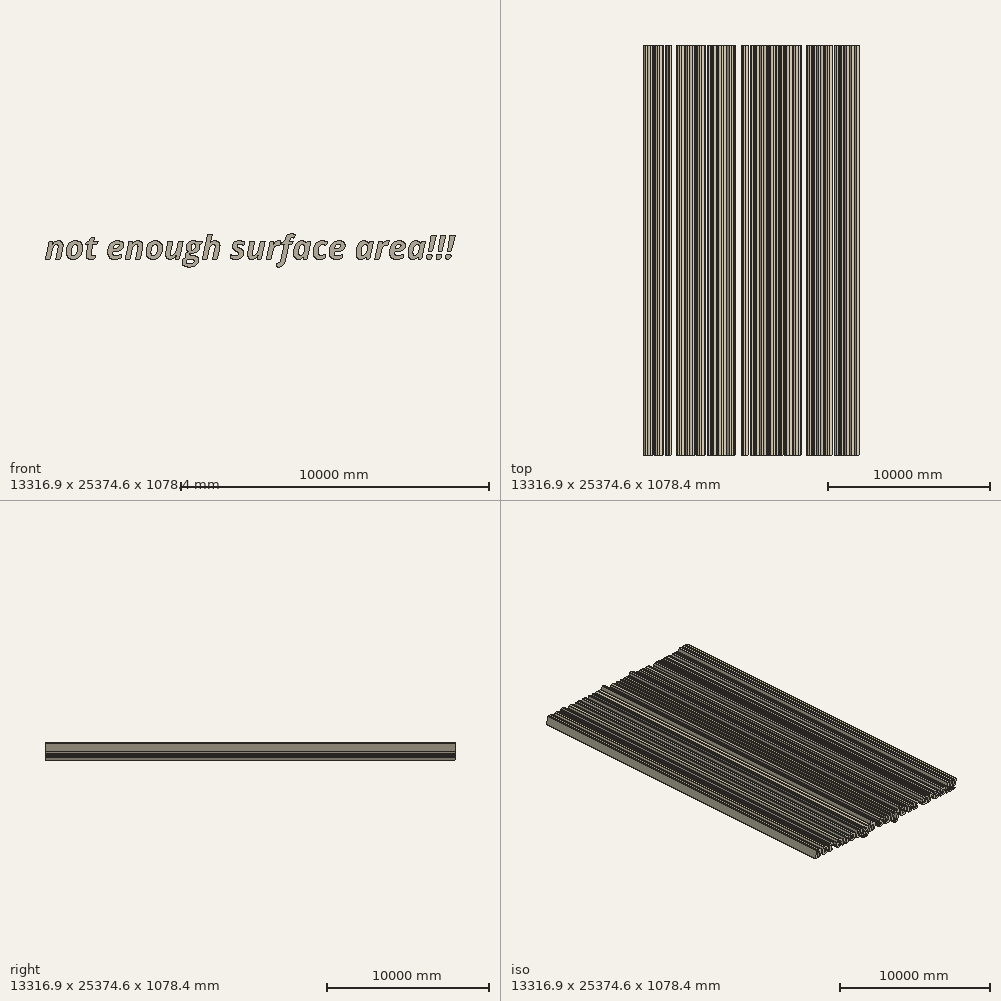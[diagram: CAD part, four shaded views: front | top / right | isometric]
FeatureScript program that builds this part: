
annotation { "Feature Type Name" : "Feature", "Feature Type Description" : "" }
export const myFeature = defineFeature(function(context is Context, id is Id, definition is map)
    precondition{}
    {
        {
            var Q0;
            Q0=qCreatedBy(makeId("Front.planeOp"),FACE);
            var sketch = newSketch(context, id + "F0", { "sketchPlane" : qUnion([Q0])});
            skText(sketch, "E0", { "text": "not enough surface area!!!", "fontName": "OpenSans-BoldItalic.ttf"});
            const initialGuessF0  = {"E0": [-0.1373, -0.14736, 1, 0, 0.77222]};
            skSetInitialGuess(sketch, initialGuessF0);
            skSolve(sketch);
        }
        {
            var Q0;
            Q0=qSketchRegion(id+"F0",true);
            extrude(context, id + "F1", {"entities" : qUnion([Q0]), "depth" : 25374.6 * mm});
        }
    });
